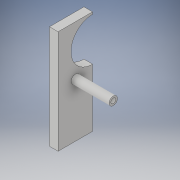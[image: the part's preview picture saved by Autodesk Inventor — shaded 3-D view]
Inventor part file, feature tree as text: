
AUTODESK INVENTOR PART (.ipt)
format: ipt  version: 2019 (Build 230136000, 136)  size: 130,560 bytes
history: native  units: in
note: dims shown in document units (in); Inventor stores cm internally (conversion verified against a paired STEP export)
features: extrude x3, sketch x3, projected_geometry x1
ambient origin geometry x8: Origin, YZ Plane, XZ Plane, XY Plane, X Axis, Y Axis, Z Axis, Center Point
bodies: Solid1 (feature_tree)
feature tree (7):
  extrude  "Extrusion1"  Depth=1.0in
  extrude  "Extrusion2"  Depth=0.625in
  extrude  "Extrusion4"  Depth=0.1in
  sketch  "Sketch1"  dims[d0=3.0in d1=1.0in]
  sketch  "Sketch2"  dims[d2=1.25in d3=0.625in]
  sketch  "Sketch4"  dims[d4=0.25in d5=0.0in d6=0.1in d7=1.0in d8=0.5in d9=0.35in d10=1.5in d11=0.0in d16=0.14in d17=0.24in d18=1.1in d19=0.0in d20=0.0625in]
  projected_geometry  "Projected Loop2"
